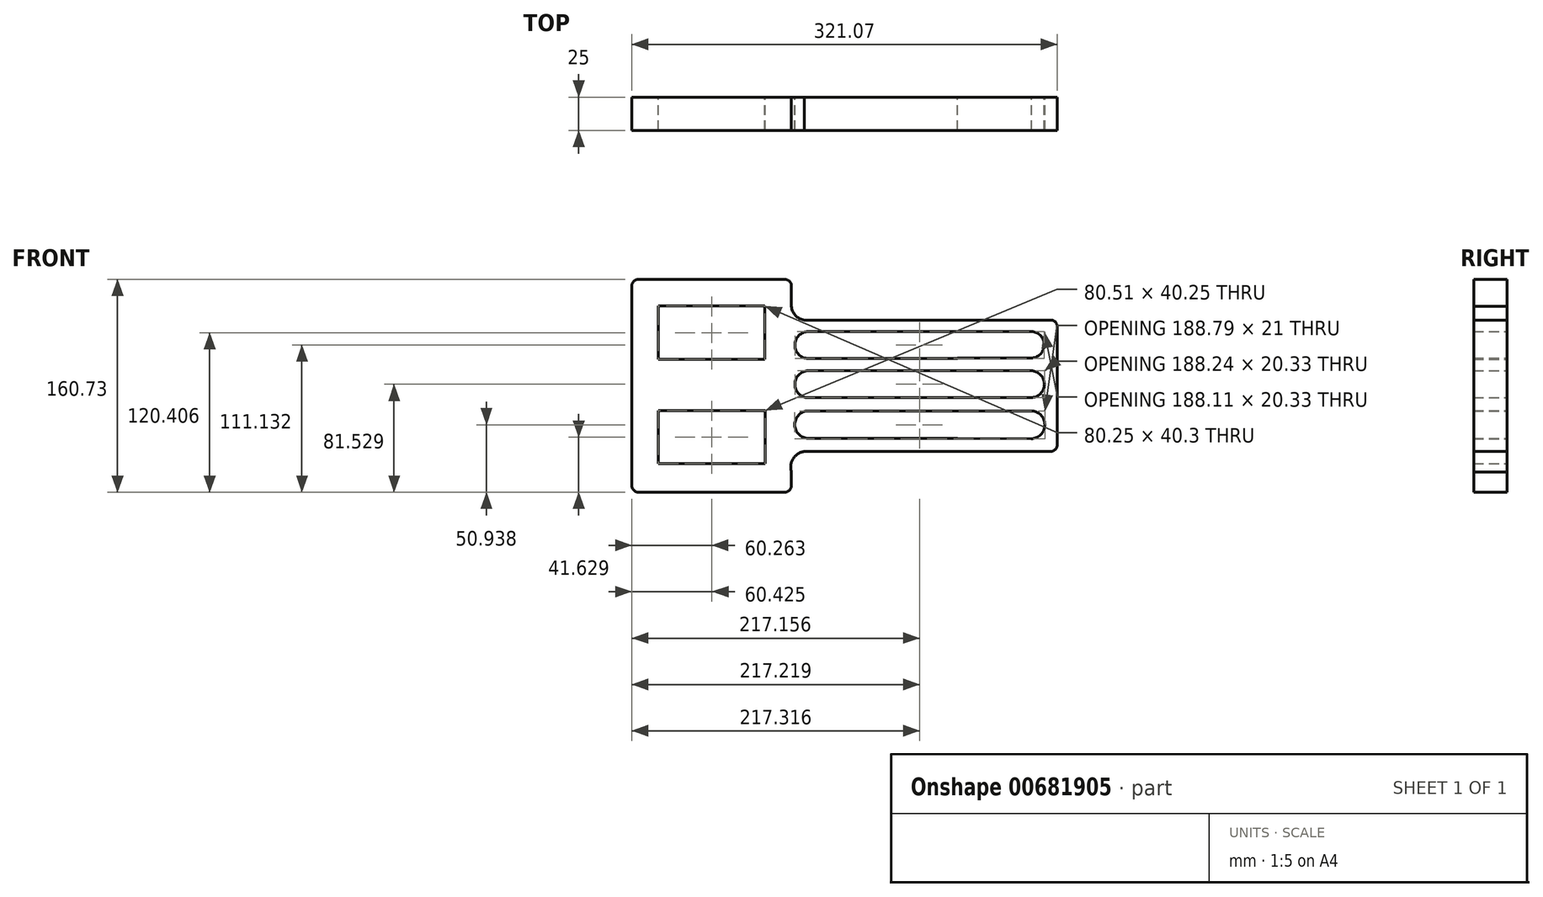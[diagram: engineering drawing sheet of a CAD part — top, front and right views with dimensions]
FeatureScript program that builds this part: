
annotation { "Feature Type Name" : "Feature", "Feature Type Description" : "" }
export const myFeature = defineFeature(function(context is Context, id is Id, definition is map)
    precondition{}
    {
        {
            var Q0;
            Q0=qCreatedBy(makeId("Front.planeOp"),FACE);
            var sketch = newSketch(context, id + "F0", { "sketchPlane" : qUnion([Q0])});
            skLineSegment(sketch, "E0", {"start": v(0, 51.27) * mm, "end": v(0, -99.46) * mm});
            skLineSegment(sketch, "E1", {"start": v(5, -104.46) * mm, "end": v(115.45, -104.46) * mm});
            skLineSegment(sketch, "E2", {"start": v(5, 56.27) * mm, "end": v(115.45, 56.27) * mm});
            skLineSegment(sketch, "E3", {"start": v(120.45, 51.27) * mm, "end": v(120.45, 36) * mm});
            skLineSegment(sketch, "E4", {"start": v(120.45, -99.46) * mm, "end": v(120.45, -89.04) * mm});
            skLineSegment(sketch, "E5", {"start": v(130.64, -73.62) * mm, "end": v(316.07, -73.62) * mm});
            skLineSegment(sketch, "E6", {"start": v(130.18, 25.56) * mm, "end": v(316.07, 25.56) * mm});
            skLineSegment(sketch, "E7", {"start": v(321.07, 20.56) * mm, "end": v(321.07, -68.62) * mm});
            skArc(sketch, "E8", {"start": v(120.45, 36) * mm, "mid": v(124.58, 28) * mm, "end": v(133.27, 25.56) * mm});
            skArc(sketch, "E9", {"start": v(133.27, -73.62) * mm, "mid": v(122.71, -77.88) * mm, "end": v(120.45, -89.04) * mm});
            skPoint(sketch, "E10.orphan", {"position": v(120.45, -73.62) * mm});
            skLineSegment(sketch, "E11", {"start": v(20.17, -82.96) * mm, "end": v(100.68, -82.96) * mm});
            skLineSegment(sketch, "E12", {"start": v(100.68, -82.96) * mm, "end": v(100.68, -42.7) * mm});
            skLineSegment(sketch, "E13", {"start": v(100.68, -42.7) * mm, "end": v(20.17, -42.7) * mm});
            skLineSegment(sketch, "E14", {"start": v(20.17, -42.7) * mm, "end": v(20.17, -82.96) * mm});
            skPoint(sketch, "E15.end.orphan", {"position": v(20.17, -72.5) * mm});
            skPoint(sketch, "E16.end.orphan", {"position": v(60.22, -82.96) * mm});
            skPoint(sketch, "E16.start.orphan", {"position": v(60.22, -104.46) * mm});
            skLineSegment(sketch, "E17", {"start": v(20.14, 36.1) * mm, "end": v(100.39, 36.1) * mm});
            skLineSegment(sketch, "E18", {"start": v(100.39, 36.1) * mm, "end": v(100.39, -4.2) * mm});
            skLineSegment(sketch, "E19", {"start": v(100.39, -4.2) * mm, "end": v(20.14, -4.2) * mm});
            skLineSegment(sketch, "E20", {"start": v(20.14, -4.2) * mm, "end": v(20.14, 36.1) * mm});
            skLineSegment(sketch, "E21", {"start": v(245.9, -33.1) * mm, "end": v(245.9, -33.02) * mm});
            skLineSegment(sketch, "E22", {"start": v(245.9, -3.5) * mm, "end": v(245.9, -3.16) * mm});
            skLineSegment(sketch, "E23", {"start": v(245.9, 16.84) * mm, "end": v(133.27, 16.84) * mm});
            skLineSegment(sketch, "E24", {"start": v(245.9, -3.5) * mm, "end": v(133.27, -3.5) * mm});
            skArc(sketch, "E25", {"start": v(133.27, 16.84) * mm, "mid": v(123.1, 6.67) * mm, "end": v(133.27, -3.5) * mm});
            skLineSegment(sketch, "E26", {"start": v(245.9, -12.77) * mm, "end": v(133.27, -12.77) * mm});
            skLineSegment(sketch, "E27", {"start": v(245.9, -33.1) * mm, "end": v(133.27, -33.1) * mm});
            skLineSegment(sketch, "E28", {"start": v(245.9, -43.08) * mm, "end": v(133.27, -43.08) * mm});
            skLineSegment(sketch, "E29", {"start": v(245.9, -63.77) * mm, "end": v(133.27, -63.77) * mm});
            skArc(sketch, "E30", {"start": v(133.27, -12.77) * mm, "mid": v(123.1, -22.93) * mm, "end": v(133.27, -33.1) * mm});
            skArc(sketch, "E31", {"start": v(133.27, -43.08) * mm, "mid": v(122.92, -53.43) * mm, "end": v(133.27, -63.77) * mm});
            skPoint(sketch, "E32.visualSharp", {"position": v(321.07, 25.56) * mm});
            skArc(sketch, "E32.filletArc", {"start": v(321.07, 20.56) * mm, "mid": v(319.6, 24.1) * mm, "end": v(316.07, 25.56) * mm});
            skPoint(sketch, "E33.visualSharp", {"position": v(321.07, -73.62) * mm});
            skArc(sketch, "E33.filletArc", {"start": v(316.07, -73.62) * mm, "mid": v(319.6, -72.15) * mm, "end": v(321.07, -68.62) * mm});
            skPoint(sketch, "E34.visualSharp", {"position": v(0, -104.46) * mm});
            skArc(sketch, "E34.filletArc", {"start": v(0, -99.46) * mm, "mid": v(1.46, -103) * mm, "end": v(5, -104.46) * mm});
            skPoint(sketch, "E35.visualSharp", {"position": v(0, 56.27) * mm});
            skArc(sketch, "E35.filletArc", {"start": v(5, 56.27) * mm, "mid": v(1.46, 54.8) * mm, "end": v(0, 51.27) * mm});
            skPoint(sketch, "E36.visualSharp", {"position": v(120.45, 56.27) * mm});
            skArc(sketch, "E36.filletArc", {"start": v(120.45, 51.27) * mm, "mid": v(118.98, 54.8) * mm, "end": v(115.45, 56.27) * mm});
            skPoint(sketch, "E37.visualSharp", {"position": v(120.45, -104.46) * mm});
            skArc(sketch, "E37.filletArc", {"start": v(115.45, -104.46) * mm, "mid": v(118.98, -103) * mm, "end": v(120.45, -99.46) * mm});
            skLineSegment(sketch, "E38", {"start": v(245.9, 16.84) * mm, "end": v(301.7, 16.84) * mm});
            skLineSegment(sketch, "E39.0", {"start": v(245.9, -3.16) * mm, "end": v(301.2, -3.16) * mm});
            skLineSegment(sketch, "E40.0", {"start": v(245.9, -33.02) * mm, "end": v(301.2, -33.02) * mm});
            skArc(sketch, "E41", {"start": v(301.2, -3.16) * mm, "mid": v(311.21, 6.6) * mm, "end": v(301.7, 16.84) * mm});
            skArc(sketch, "E42", {"start": v(301.21, -64.02) * mm, "mid": v(311.71, -53.52) * mm, "end": v(301.21, -43.02) * mm});
            skLineSegment(sketch, "E43", {"start": v(245.9, -12.77) * mm, "end": v(301.2, -12.77) * mm});
            skArc(sketch, "E44", {"start": v(301.2, -33.02) * mm, "mid": v(311.34, -22.9) * mm, "end": v(301.2, -12.77) * mm});
            skLineSegment(sketch, "E45", {"start": v(245.9, -43.08) * mm, "end": v(301.21, -43.02) * mm});
            skLineSegment(sketch, "E46", {"start": v(245.9, -63.77) * mm, "end": v(301.21, -64.02) * mm});
            skSolve(sketch);
        }
        {
            var Q0;
            Q0 = qSketchRegion(id + "F0", true);
            extrude(context, id + "F1", {"entities" : qUnion([Q0]), "depth" : 25 * mm, "offsetDistance" : 25 * mm});
        }
    });
